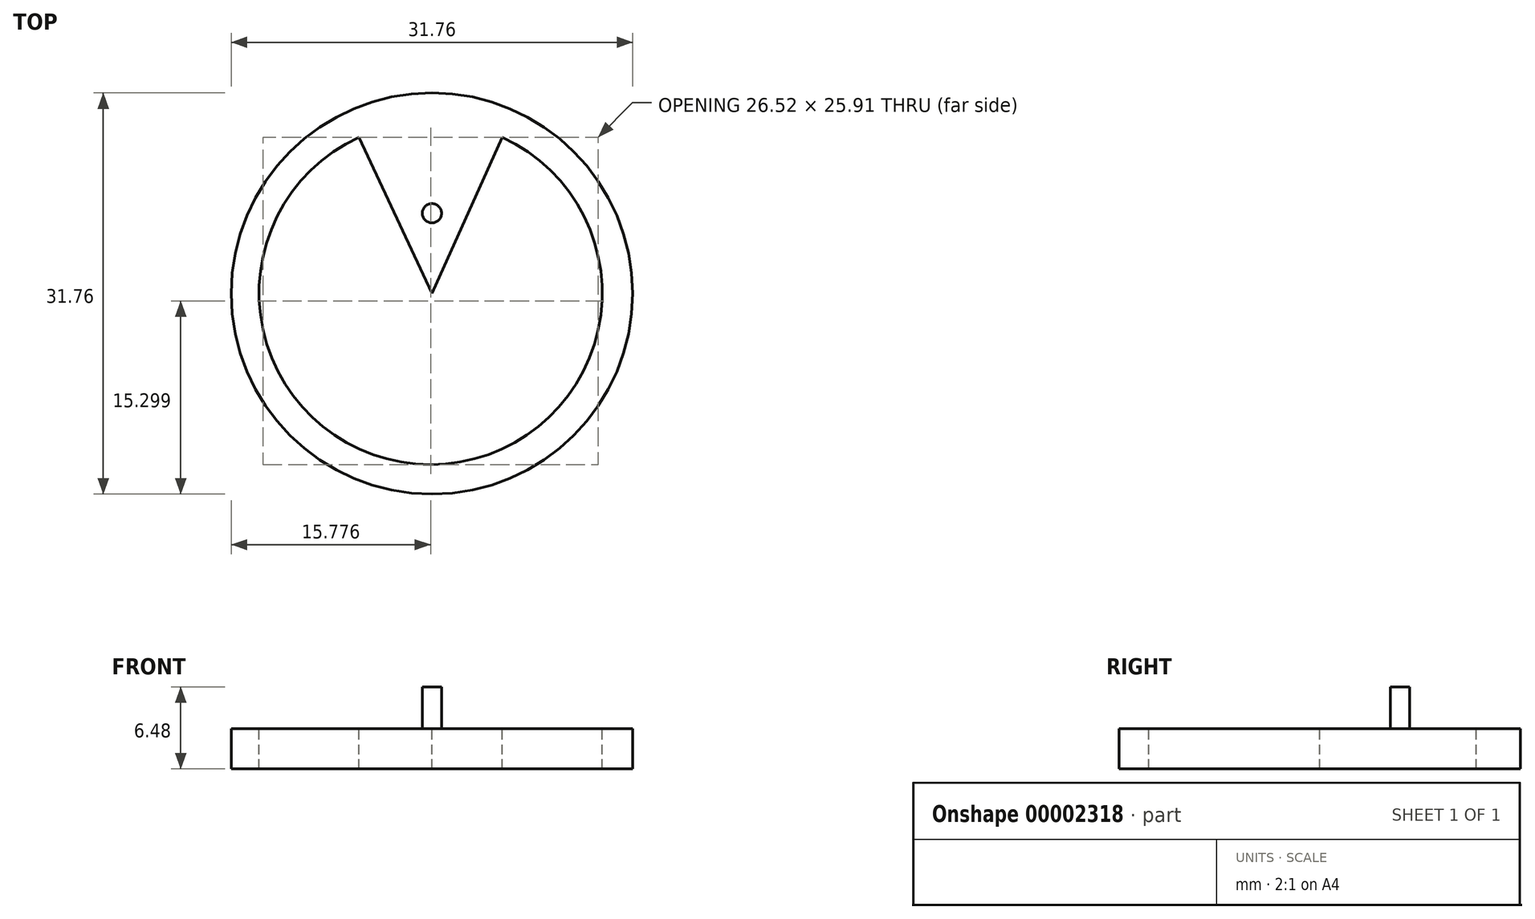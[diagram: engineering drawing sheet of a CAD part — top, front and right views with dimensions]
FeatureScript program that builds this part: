
annotation { "Feature Type Name" : "Feature", "Feature Type Description" : "" }
export const myFeature = defineFeature(function(context is Context, id is Id, definition is map)
    precondition{}
    {
        {
            var Q0;
            Q0=qCreatedBy(makeId("Top.planeOp"),FACE);
            var sketch = newSketch(context, id + "F0", { "sketchPlane" : qUnion([Q0])});
            skCircle(sketch, "E0", {"center": v(0, 0) * mm, "radius": 38.1 * mm});
            skSolve(sketch);
        }
        {
            var Q0;
            Q0=makeQuery(id+"F0.imprint","IMPRINT",FACE,{"disambiguationData":[TD([[makeQuery(id+"F0.imprint","IMPRINT",EDGE,{"derivedFrom":sQuery(id+"F0.wireOp",EDGE,"E0")}),1.0]])]});
            extrude(context, id + "F1", {"entities" : qUnion([Q0]), "depth" : 3.17 * mm});
        }
        {
            var Q0;
            Q0=makeQuery(id+"F1.opExtrude","CAP_FACE",FACE,{"disambiguationData":[OSD([sQuery(id+"F0.wireOp",EDGE,"E0")])],"isStart":false});
            var sketch = newSketch(context, id + "F2", { "sketchPlane" : qUnion([Q0])});
            skCircle(sketch, "E1", {"center": v(0, 6.35) * mm, "radius": 0.76 * mm});
            skCircle(sketch, "E2", {"center": v(0, 24.13) * mm, "radius": 1 * mm});
            skSolve(sketch);
        }
        {
            var Q0;
            {Q0=qUnion([makeQuery(id+"F2.imprint","IMPRINT",FACE,{"disambiguationData":[TD([[makeQuery(id+"F2.imprint","IMPRINT",EDGE,{"derivedFrom":sQuery(id+"F2.wireOp",EDGE,"E1")}),1.0]])]}),makeQuery(id+"F2.imprint","IMPRINT",FACE,{"disambiguationData":[TD([[makeQuery(id+"F2.imprint","IMPRINT",EDGE,{"derivedFrom":sQuery(id+"F2.wireOp",EDGE,"E2")}),1.0]])]})]);}
            extrude(context, id + "F3", {"entities" : qUnion([Q0]), "operationType" : NewBodyOperationType.ADD, "depth" : 3.3 * mm});
        }
        {
            var Q0;
            Q0=qCreatedBy(makeId("Top.planeOp"),FACE);
            var sketch = newSketch(context, id + "F4", { "sketchPlane" : qUnion([Q0])});
            skCircle(sketch, "E3", {"center": v(0, 0) * mm, "radius": 15.88 * mm});
            skSolve(sketch);
        }
        {
            var Q0;
            Q0=makeQuery(id+"F4.imprint","IMPRINT",FACE,{"disambiguationData":[TD([[makeQuery(id+"F4.imprint","IMPRINT",EDGE,{"derivedFrom":sQuery(id+"F4.wireOp",EDGE,"E3")}),1.0]])]});
            var Q1;
            Q1=makeQuery(id+"F3.opExtrude","CAP_FACE",FACE,{"disambiguationData":[OSD([sQuery(id+"F2.wireOp",EDGE,"E1")])],"isStart":false});
            extrude(context, id + "F5", {"entities" : qUnion([Q0]), "endBound" : BoundingType.UP_TO_SURFACE, "endBoundEntityFace" : qUnion([Q1]), "depth" : 25.4 * mm});
        }
        {
            var Q0;
            Q0=makeQuery(id+"F1.opExtrude","SWEPT_BODY",BODY,{"disambiguationData":[OSD([sQuery(id+"F0.wireOp",EDGE,"E0")])]});
            var Q1;
            Q1=makeQuery(id+"F5.opExtrude","SWEPT_BODY",BODY,{"disambiguationData":[OSD([sQuery(id+"F4.wireOp",EDGE,"E3")])]});
            booleanBodies(context, id + "F6", {"operationType" : BooleanOperationType.INTERSECTION, "tools" : qUnion([Q0, Q1])});
        }
        {
            var Q0;
            Q0=makeQuery(id+"F1.opExtrude","CAP_FACE",FACE,{"disambiguationData":[OSD([sQuery(id+"F0.wireOp",EDGE,"E0")])],"isStart":false});
            var sketch = newSketch(context, id + "F7", { "sketchPlane" : qUnion([Q0])});
            skLineSegment(sketch, "E4", {"start": v(0, 0) * mm, "end": v(-5.76, 12.37) * mm});
            skLineSegment(sketch, "E5", {"start": v(0, 0) * mm, "end": v(5.55, 12.37) * mm});
            skArc(sketch, "E6", {"start": v(-5.76, 12.37) * mm, "mid": v(-0.1, -13.54) * mm, "end": v(5.55, 12.37) * mm});
            skSolve(sketch);
        }
        {
            var Q0;
            Q0=makeQuery(id+"F7.imprint","IMPRINT",FACE,{"disambiguationData":[TD([[makeQuery(id+"F7.imprint","IMPRINT",EDGE,{"derivedFrom":sQuery(id+"F7.wireOp",EDGE,"E4")}),1.0]])]});
            extrude(context, id + "F8", {"entities" : qUnion([Q0]), "operationType" : NewBodyOperationType.REMOVE, "oppositeDirection" : true, "depth" : 25.4 * mm});
        }
    });
